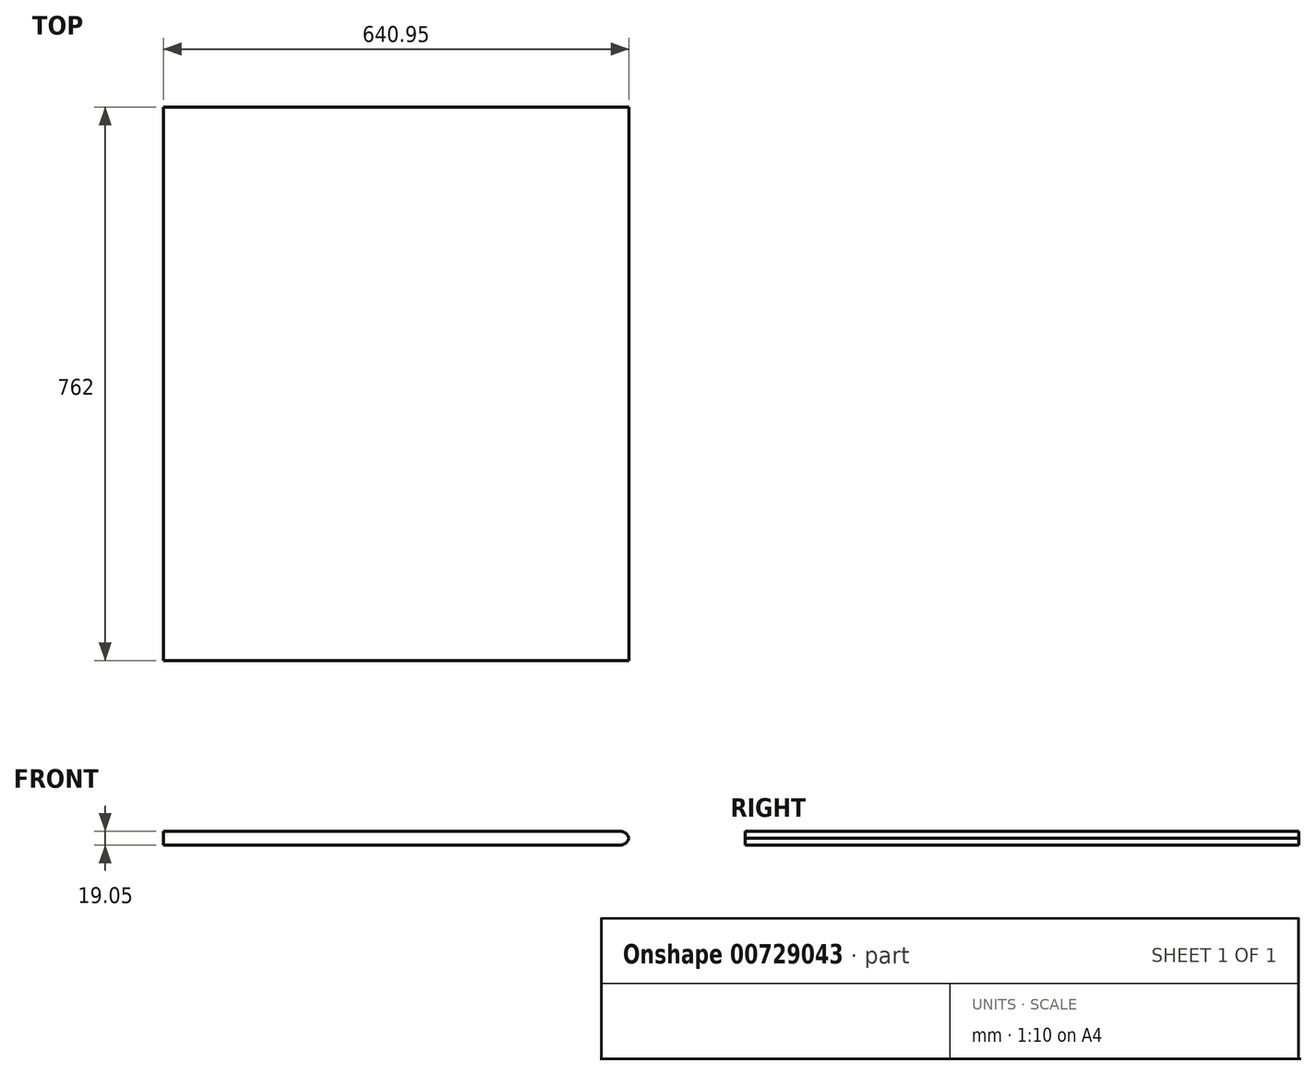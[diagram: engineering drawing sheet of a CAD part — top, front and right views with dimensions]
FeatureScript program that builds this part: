
annotation { "Feature Type Name" : "Feature", "Feature Type Description" : "" }
export const myFeature = defineFeature(function(context is Context, id is Id, definition is map)
    precondition{}
    {
        {
            var Q0;
            Q0=qCreatedBy(makeId("Top.planeOp"),FACE);
            var sketch = newSketch(context, id + "F0", { "sketchPlane" : qUnion([Q0])});
            skLineSegment(sketch, "E0.bottom", {"start": v(320.68, 381) * mm, "end": v(-320.68, 381) * mm});
            skLineSegment(sketch, "E0.top", {"start": v(320.68, -381) * mm, "end": v(-320.68, -381) * mm});
            skLineSegment(sketch, "E0.left", {"start": v(320.68, 381) * mm, "end": v(320.68, -381) * mm});
            skLineSegment(sketch, "E0.right", {"start": v(-320.68, 381) * mm, "end": v(-320.68, -381) * mm});
            skPoint(sketch, "E0.middle", {"position": v(0, 0) * mm});
            skSolve(sketch);
        }
        {
            var Q0;
            Q0 = qSketchRegion(id + "F0", true);
            extrude(context, id + "F1", {"entities" : qUnion([Q0]), "depth" : 19.05 * mm, "offsetDistance" : 25.4 * mm});
        }
        {
            var Q0;
            Q0=makeQuery(id+"F1.opExtrude","CAP_EDGE",EDGE,{"disambiguationData":[OSD([sQuery(id+"F0.wireOp",EDGE,"E0.left")])],"isStart":false});
            var Q1;
            Q1=makeQuery(id+"F1.opExtrude","CAP_EDGE",EDGE,{"disambiguationData":[OSD([sQuery(id+"F0.wireOp",EDGE,"E0.left")])],"isStart":true});
            fillet(context, id + "F2", {"entities" : qUnion([Q0, Q1]), "radius" : 12.7 * mm, "tangentPropagation" : true, "allowEdgeOverflow" : false});
        }
    });
